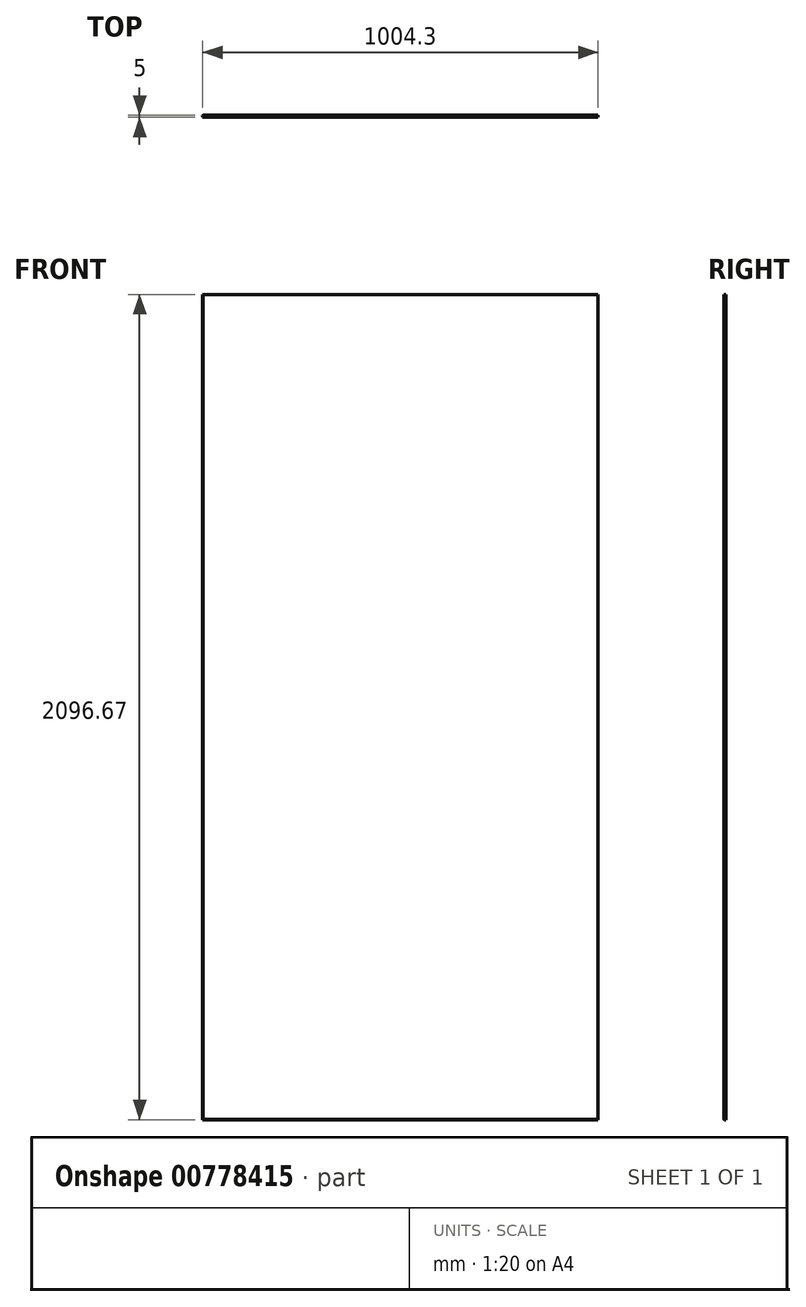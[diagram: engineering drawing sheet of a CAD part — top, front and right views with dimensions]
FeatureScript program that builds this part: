
annotation { "Feature Type Name" : "Feature", "Feature Type Description" : "" }
export const myFeature = defineFeature(function(context is Context, id is Id, definition is map)
    precondition{}
    {
        {
            var Q0;
            Q0=qCreatedBy(makeId("Front.planeOp"),FACE);
            var sketch = newSketch(context, id + "F0", { "sketchPlane" : qUnion([Q0])});
            skLineSegment(sketch, "E0.bottom", {"start": v(502.14, 0) * mm, "end": v(-502.14, 0) * mm});
            skLineSegment(sketch, "E0.top", {"start": v(502.15, 2096.67) * mm, "end": v(-502.14, 2096.67) * mm});
            skLineSegment(sketch, "E0.left", {"start": v(502.14, 0) * mm, "end": v(502.14, 2096.67) * mm});
            skLineSegment(sketch, "E0.right", {"start": v(-502.14, 0) * mm, "end": v(-502.14, 2096.67) * mm});
            skPoint(sketch, "E0.middle", {"position": v(0, 1048.34) * mm});
            skSolve(sketch);
        }
        {
            var Q0;
            Q0=makeQuery(id+"F0.imprint","IMPRINT",FACE,{"disambiguationData":[TD([[makeQuery(id+"F0.imprint","IMPRINT",EDGE,{"derivedFrom":sQuery(id+"F0.wireOp",EDGE,"E0.bottom")}),-1.0]])]});
            extrude(context, id + "F1", {"entities" : qUnion([Q0]), "endBound" : BoundingType.SYMMETRIC, "depth" : 5 * mm, "offsetDistance" : 25 * mm});
        }
        {
            var Q0;
            Q0=makeQuery(id+"F1.opExtrude","CAP_EDGE",EDGE,{"disambiguationData":[OSD([sQuery(id+"F0.wireOp",EDGE,"E0.bottom")])],"isStart":false});
            var Q1;
            Q1=makeQuery(id+"F1.opExtrude","CAP_EDGE",EDGE,{"disambiguationData":[OSD([sQuery(id+"F0.wireOp",EDGE,"E0.left")])],"isStart":false});
            var Q2;
            Q2=makeQuery(id+"F1.opExtrude","CAP_EDGE",EDGE,{"disambiguationData":[OSD([sQuery(id+"F0.wireOp",EDGE,"E0.top")])],"isStart":false});
            var Q3;
            Q3=makeQuery(id+"F1.opExtrude","CAP_EDGE",EDGE,{"disambiguationData":[OSD([sQuery(id+"F0.wireOp",EDGE,"E0.right")])],"isStart":false});
            var Q4;
            Q4=makeQuery(id+"F1.opExtrude","CAP_EDGE",EDGE,{"disambiguationData":[OSD([sQuery(id+"F0.wireOp",EDGE,"E0.right")])],"isStart":true});
            var Q5;
            Q5=makeQuery(id+"F1.opExtrude","CAP_EDGE",EDGE,{"disambiguationData":[OSD([sQuery(id+"F0.wireOp",EDGE,"E0.top")])],"isStart":true});
            var Q6;
            Q6=makeQuery(id+"F1.opExtrude","CAP_EDGE",EDGE,{"disambiguationData":[OSD([sQuery(id+"F0.wireOp",EDGE,"E0.left")])],"isStart":true});
            var Q7;
            Q7=makeQuery(id+"F1.opExtrude","CAP_EDGE",EDGE,{"disambiguationData":[OSD([sQuery(id+"F0.wireOp",EDGE,"E0.bottom")])],"isStart":true});
            chamfer(context, id + "F2", {"entities" : qUnion([Q0, Q1, Q2, Q3, Q4, Q5, Q6, Q7]), "chamferType" : ChamferType.TWO_OFFSETS, "width1" : 0.5 * mm, "oppositeDirection" : false, "width2" : 0.5 * mm, "tangentPropagation" : true});
        }
    });
